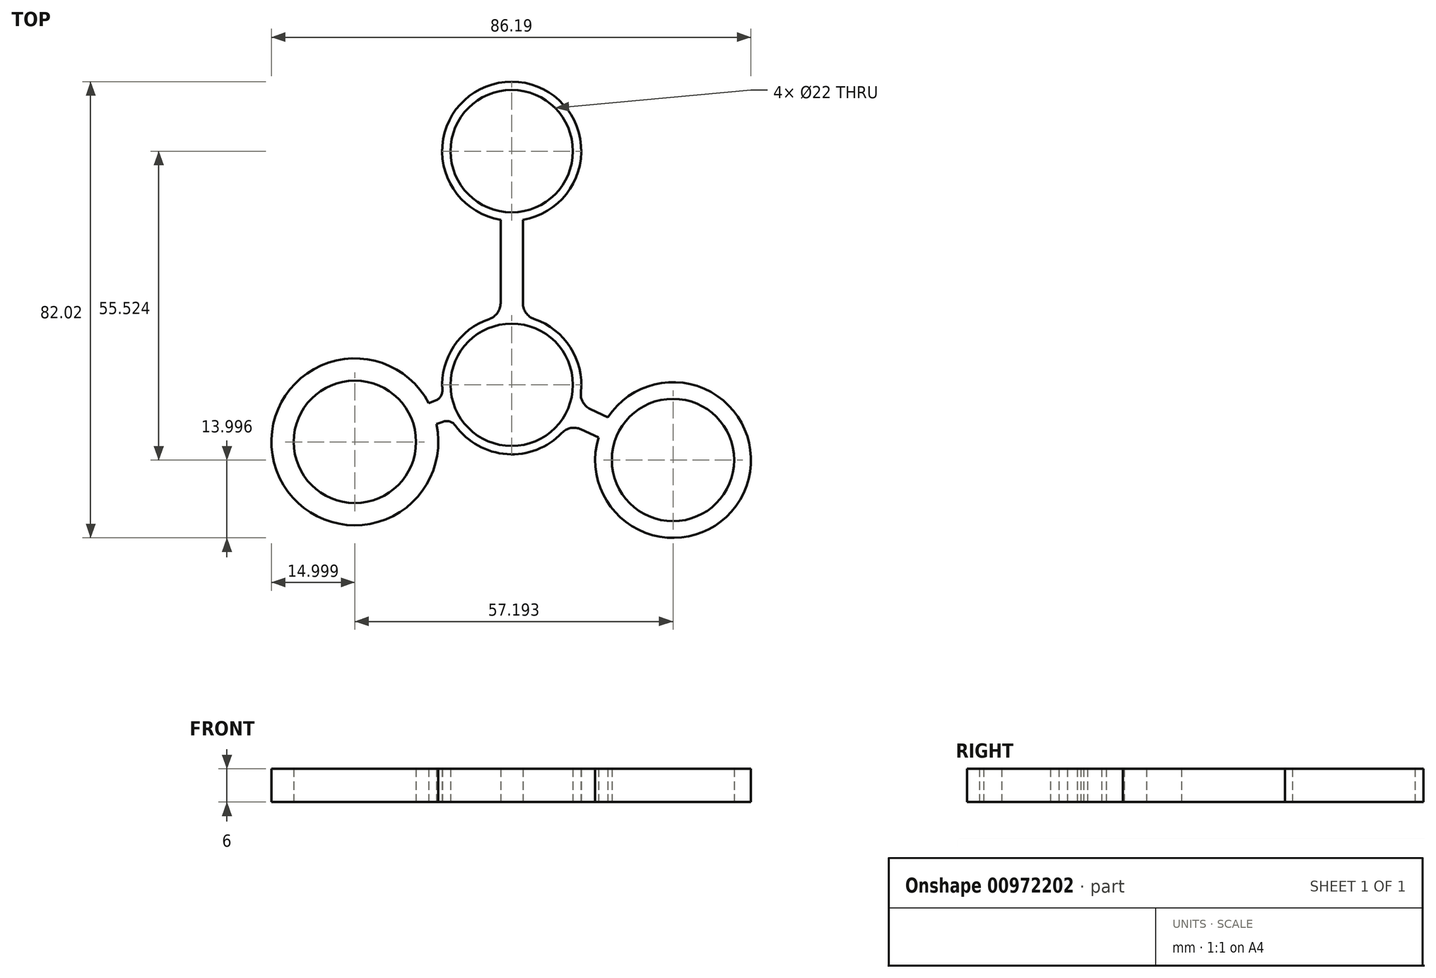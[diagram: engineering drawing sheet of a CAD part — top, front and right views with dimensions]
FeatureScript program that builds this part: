
annotation { "Feature Type Name" : "Feature", "Feature Type Description" : "" }
export const myFeature = defineFeature(function(context is Context, id is Id, definition is map)
    precondition{}
    {
        {
            var Q0;
            Q0=qCreatedBy(makeId("Top.planeOp"),FACE);
            var sketch = newSketch(context, id + "F0", { "sketchPlane" : qUnion([Q0])});
            skArc(sketch, "E0", {"start": v(-4.03, 11.83) * mm, "mid": v(-10.41, 6.92) * mm, "end": v(-12.47, -0.87) * mm});
            skCircle(sketch, "E1", {"center": v(0, 0) * mm, "radius": 11 * mm});
            skArc(sketch, "E2", {"start": v(2, 29.66) * mm, "mid": v(0, 54.5) * mm, "end": v(-2, 29.66) * mm});
            skCircle(sketch, "E3", {"center": v(0, 42) * mm, "radius": 11 * mm});
            skLineSegment(sketch, "E4", {"start": v(2, 29.66) * mm, "end": v(2, 14.67) * mm});
            skLineSegment(sketch, "E5", {"start": v(-2, 29.66) * mm, "end": v(-2, 14.67) * mm});
            skArc(sketch, "E6", {"start": v(15.6, -9.48) * mm, "mid": v(41.7, -19.44) * mm, "end": v(17.29, -5.86) * mm});
            skCircle(sketch, "E7", {"center": v(29, -13.52) * mm, "radius": 11 * mm});
            skPoint(sketch, "E8.visualSharp", {"position": v(-2, 12.34) * mm});
            skArc(sketch, "E8.filletArc", {"start": v(-4.03, 11.83) * mm, "mid": v(-2.56, 12.93) * mm, "end": v(-2, 14.67) * mm});
            skPoint(sketch, "E9.visualSharp", {"position": v(2, 12.34) * mm});
            skArc(sketch, "E9.filletArc", {"start": v(2, 14.67) * mm, "mid": v(2.56, 12.93) * mm, "end": v(4.03, 11.83) * mm});
            skLineSegment(sketch, "E10.trimOffspring", {"start": v(14.14, -4.39) * mm, "end": v(17.29, -5.86) * mm});
            skLineSegment(sketch, "E11.trimOffspring", {"start": v(12.45, -8.01) * mm, "end": v(15.6, -9.48) * mm});
            skArc(sketch, "E12.trimOffspring", {"start": v(12.43, -1.35) * mm, "mid": v(10.54, 6.72) * mm, "end": v(4.03, 11.83) * mm});
            skArc(sketch, "E13.MirrorCS", {"start": v(-13.54, -7.06) * mm, "mid": v(-42.29, -15.4) * mm, "end": v(-14.9, -3.3) * mm});
            skLineSegment(sketch, "E14.MirrorCS", {"start": v(-13.78, -2.89) * mm, "end": v(-14.9, -3.3) * mm});
            skLineSegment(sketch, "E15.MirrorCS", {"start": v(-12.41, -6.65) * mm, "end": v(-13.54, -7.06) * mm});
            skCircle(sketch, "E16", {"center": v(-28.2, -10.26) * mm, "radius": 11 * mm});
            skArc(sketch, "E17.trimOffspring", {"start": v(-10.11, -7.35) * mm, "mid": v(-0.85, -12.47) * mm, "end": v(9.02, -8.65) * mm});
            skPoint(sketch, "E18.visualSharp", {"position": v(-12.28, -2.34) * mm});
            skArc(sketch, "E18.filletArc", {"start": v(-13.78, -2.89) * mm, "mid": v(-12.79, -2.1) * mm, "end": v(-12.47, -0.87) * mm});
            skPoint(sketch, "E19.visualSharp", {"position": v(12.03, -3.4) * mm});
            skArc(sketch, "E19.filletArc", {"start": v(12.43, -1.35) * mm, "mid": v(12.8, -3.14) * mm, "end": v(14.14, -4.39) * mm});
            skPoint(sketch, "E20.visualSharp", {"position": v(10.34, -7.03) * mm});
            skArc(sketch, "E20.filletArc", {"start": v(12.45, -8.01) * mm, "mid": v(10.63, -7.78) * mm, "end": v(9.02, -8.65) * mm});
            skLineSegment(sketch, "E21", {"start": v(0, 0) * mm, "end": v(-28.2, -10.26) * mm, "construction": true});
            skLineSegment(sketch, "E22", {"start": v(0, 0) * mm, "end": v(29, -13.52) * mm, "construction": true});
            skPoint(sketch, "E23.visualSharp", {"position": v(-10.91, -6.1) * mm});
            skArc(sketch, "E23.filletArc", {"start": v(-10.11, -7.35) * mm, "mid": v(-11.14, -6.61) * mm, "end": v(-12.41, -6.65) * mm});
            skSolve(sketch);
        }
        {
            var Q0;
            Q0=makeQuery(id+"F0.imprint","IMPRINT",FACE,{"disambiguationData":[TD([[makeQuery(id+"F0.imprint","IMPRINT",EDGE,{"derivedFrom":sQuery(id+"F0.wireOp",EDGE,"E0")}),1.0]])]});
            extrude(context, id + "F1", {"entities" : qUnion([Q0]), "endBound" : BoundingType.SYMMETRIC, "depth" : 6 * mm, "offsetDistance" : 25 * mm});
        }
    });
